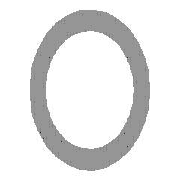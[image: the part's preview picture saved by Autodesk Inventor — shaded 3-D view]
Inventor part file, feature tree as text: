
AUTODESK INVENTOR PART (.ipt)
format: ipt  version: 2021 (Build 250183000, 183)  size: 159,744 bytes
history: native  units: mm (DEFAULTED — no unit token found)
features: other x10, sketch x4, extrude x2, plane x1
ambient origin geometry x8: Origin, YZ Plane, XZ Plane, XY Plane, X Axis, Y Axis, Z Axis, Center Point
bodies: Solid1 (feature_tree)
feature tree (17):
  parser-record x1  (decoder bookkeeping rows leaked as tree rows — omitted from the tree; the rows remain in map.json)
  other  "Driven Length"
  other  "Plano inicial"
  other  "Plano final"
  extrude  "Cuerpo"  Depth=4.8514mm
  extrude  "Extrusión2"  TaperAngle=0.0deg  [1 undecoded]
  sketch  "Boceto"  dims[d6=90.0deg d7=550.0mm d84=5.0mm d85=40.0mm d86=0.0mm d163=5.0mm d164=0.0mm d165=5.0mm d166=0.0mm]
  sketch  "Sketch3"  dims[d0=42.164mm d1=4.8514mm]
  plane  "Work Plane3"
  sketch  "Sketch4"  dims[d2=528.33989mm d3=0.0mm d4=-0.0mm]
  sketch  "Boceto5"  dims[d5=550.0mm]
  other  "Sup116"
  other  "Sup117"
  other  "Sólido40"
  other  "Sup115"
  other  "Superficie de contorno77"
  other  "Superficie de contorno78"
note: 1 required parameter value undecoded (feature->parameter linkage not recoverable at this tier; creation-order binding heuristic only, values carry confidence <= 0.55)
